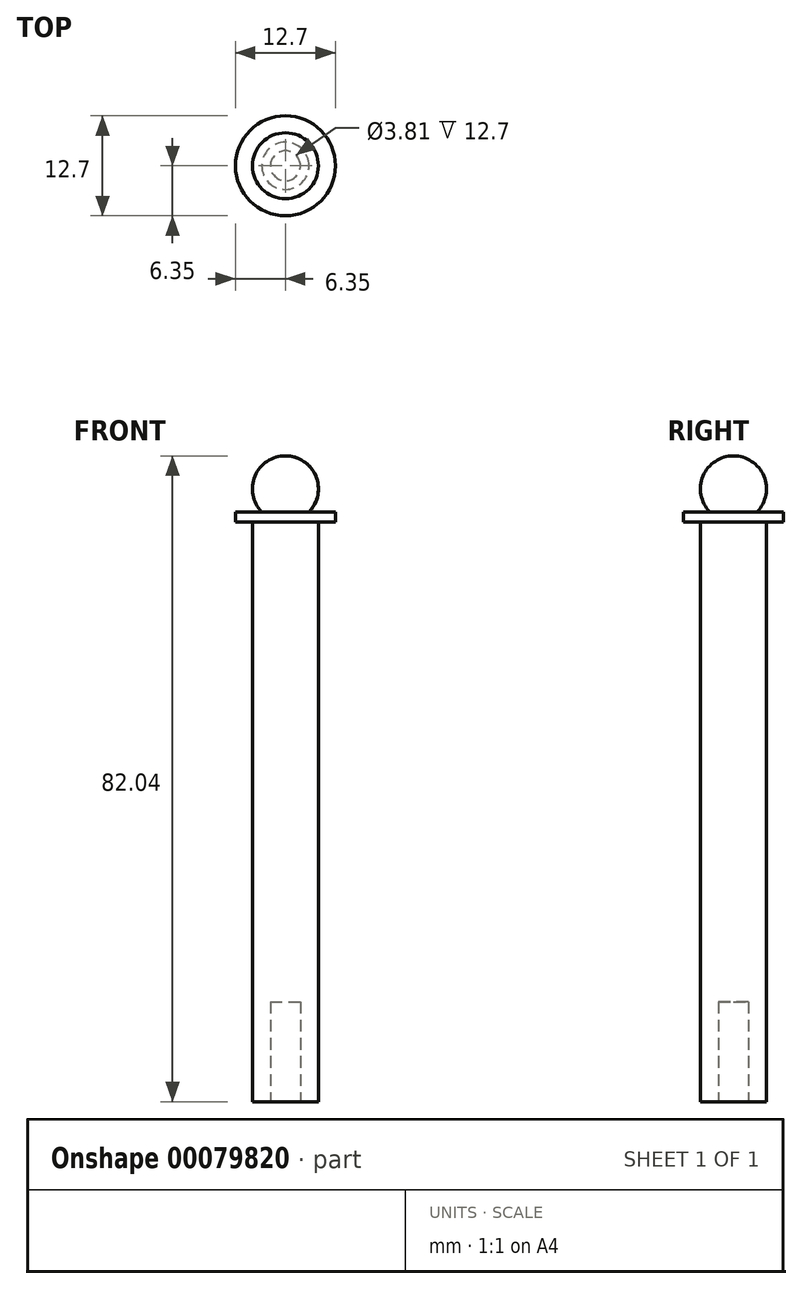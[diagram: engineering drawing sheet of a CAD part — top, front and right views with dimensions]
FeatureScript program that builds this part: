
annotation { "Feature Type Name" : "Feature", "Feature Type Description" : "" }
export const myFeature = defineFeature(function(context is Context, id is Id, definition is map)
    precondition{}
    {
        {
            var Q0;
            Q0=qCreatedBy(makeId("Top.planeOp"),FACE);
            var sketch = newSketch(context, id + "F0", { "sketchPlane" : qUnion([Q0])});
            skCircle(sketch, "E0", {"center": v(0, 0) * mm, "radius": 4.2 * mm});
            skSolve(sketch);
        }
        {
            var Q0;
            Q0 = qSketchRegion(id + "F0", true);
            extrude(context, id + "F1", {"entities" : qUnion([Q0]), "depth" : 73.66 * mm});
        }
        {
            var Q0;
            Q0=makeQuery(id+"F1.opExtrude","CAP_FACE",FACE,{"disambiguationData":[OSD([sQuery(id+"F0.wireOp",EDGE,"E0")])],"isStart":false});
            var sketch = newSketch(context, id + "F2", { "sketchPlane" : qUnion([Q0])});
            skCircle(sketch, "E1", {"center": v(0, 0) * mm, "radius": 4.2 * mm});
            skSolve(sketch);
        }
        {
            var Q0;
            Q0 = qSketchRegion(id + "F2", true);
            extrude(context, id + "F3", {"entities" : qUnion([Q0]), "depth" : 8.38 * mm});
        }
        {
            var Q0;
            Q0=makeQuery(id+"F3.opExtrude","CAP_EDGE",EDGE,{"disambiguationData":[OSD([sQuery(id+"F2.wireOp",EDGE,"E1")])],"isStart":true});
            var Q1;
            Q1=makeQuery(id+"F3.opExtrude","CAP_EDGE",EDGE,{"disambiguationData":[OSD([sQuery(id+"F2.wireOp",EDGE,"E1")])],"isStart":false});
            fillet(context, id + "F4", {"entities" : qUnion([Q0, Q1]), "radius" : 4.2 * mm, "tangentPropagation" : true, "allowEdgeOverflow" : false});
        }
        {
            var Q0;
            Q0=makeQuery(id+"F1.opExtrude","CAP_FACE",FACE,{"disambiguationData":[OSD([sQuery(id+"F0.wireOp",EDGE,"E0")])],"isStart":false});
            var sketch = newSketch(context, id + "F5", { "sketchPlane" : qUnion([Q0])});
            skCircle(sketch, "E2", {"center": v(0, 0) * mm, "radius": 6.35 * mm});
            skSolve(sketch);
        }
        {
            var Q0;
            Q0 = qSketchRegion(id + "F5", true);
            extrude(context, id + "F6", {"entities" : qUnion([Q0]), "operationType" : NewBodyOperationType.ADD, "depth" : 1.27 * mm});
        }
        {
            var Q0;
            Q0=makeQuery(id+"F1.opExtrude","CAP_FACE",FACE,{"disambiguationData":[OSD([sQuery(id+"F0.wireOp",EDGE,"E0")])],"isStart":true});
            var sketch = newSketch(context, id + "F7", { "sketchPlane" : qUnion([Q0])});
            skCircle(sketch, "E3", {"center": v(0, 0) * mm, "radius": 1.9 * mm});
            skSolve(sketch);
        }
        {
            var Q0;
            Q0 = qSketchRegion(id + "F7", true);
            extrude(context, id + "F8", {"entities" : qUnion([Q0]), "operationType" : NewBodyOperationType.REMOVE, "oppositeDirection" : true, "depth" : 12.7 * mm});
        }
    });
